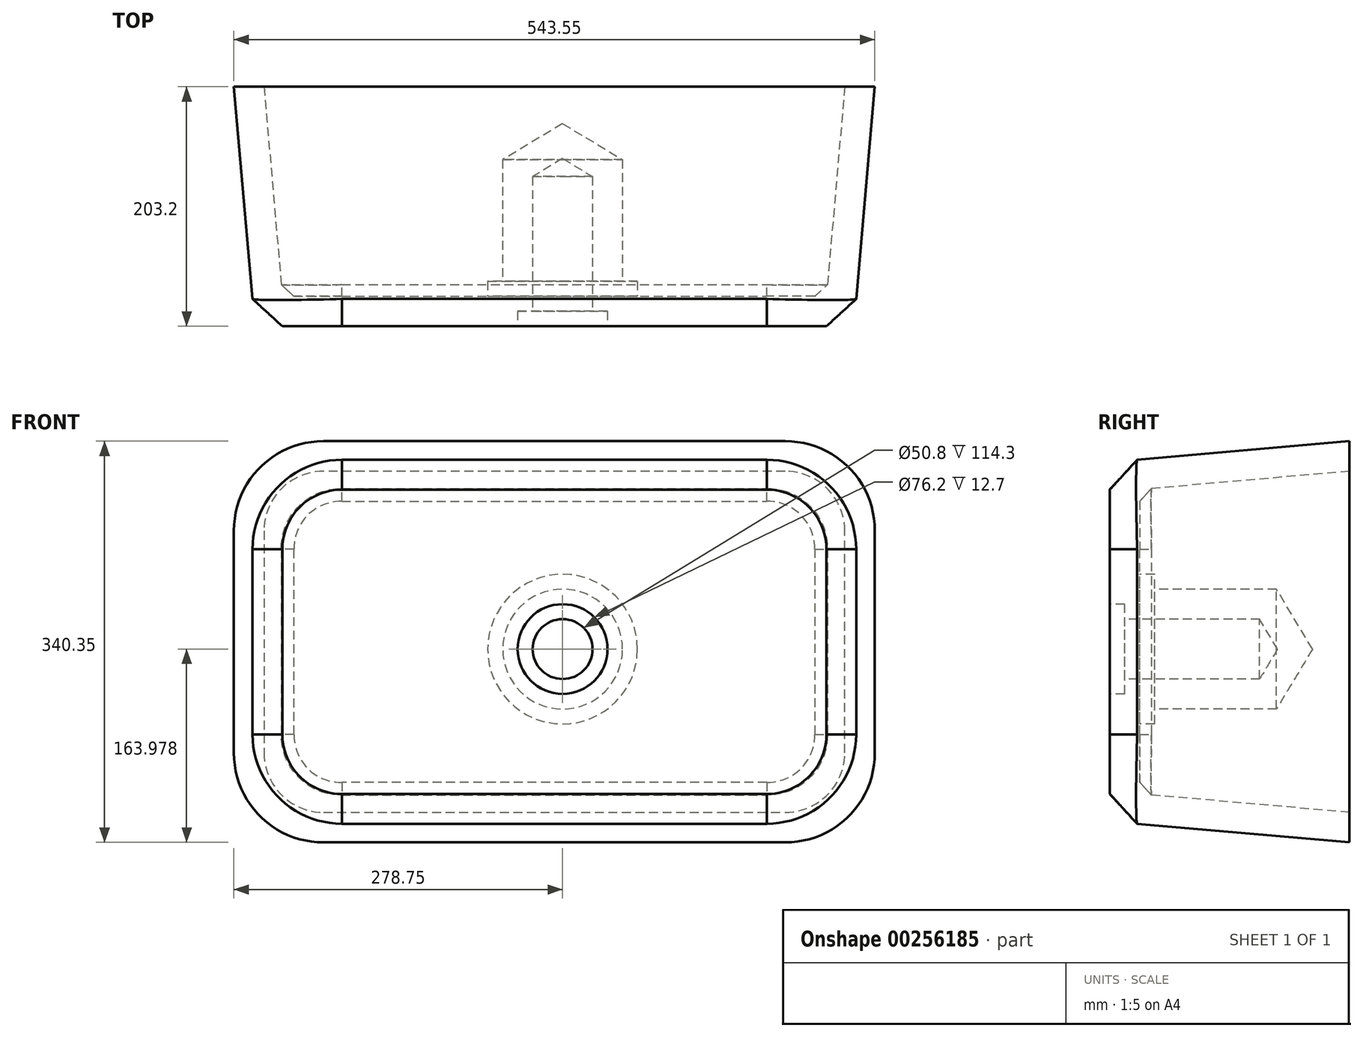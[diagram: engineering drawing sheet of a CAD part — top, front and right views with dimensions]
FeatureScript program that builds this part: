
annotation { "Feature Type Name" : "Feature", "Feature Type Description" : "" }
export const myFeature = defineFeature(function(context is Context, id is Id, definition is map)
    precondition{}
    {
        {
            var Q0;
            Q0=qCreatedBy(makeId("Front.planeOp"),FACE);
            var sketch = newSketch(context, id + "F0", { "sketchPlane" : qUnion([Q0])});
            skLineSegment(sketch, "E0.bottom", {"start": v(-260.97, 124.12) * mm, "end": v(247.03, 124.12) * mm});
            skLineSegment(sketch, "E0.top", {"start": v(-260.97, -180.68) * mm, "end": v(247.03, -180.68) * mm});
            skLineSegment(sketch, "E0.left", {"start": v(-260.97, 124.12) * mm, "end": v(-260.97, -180.68) * mm});
            skLineSegment(sketch, "E0.right", {"start": v(247.03, 124.12) * mm, "end": v(247.03, -180.68) * mm});
            skCircle(sketch, "E1", {"center": v(0, -34.47) * mm, "radius": 76.2 * mm});
            skSolve(sketch);
        }
        {
            var Q0;
            Q0=makeQuery(id+"F0.imprint","IMPRINT",FACE,{"disambiguationData":[TD([[makeQuery(id+"F0.imprint","IMPRINT",EDGE,{"derivedFrom":sQuery(id+"F0.wireOp",EDGE,"E0.bottom")}),-1.0]])]});
            var Q1;
            Q1=makeQuery(id+"F0.imprint","IMPRINT",FACE,{"disambiguationData":[TD([[makeQuery(id+"F0.imprint","IMPRINT",EDGE,{"derivedFrom":sQuery(id+"F0.wireOp",EDGE,"E1")}),1.0]])]});
            extrude(context, id + "F1", {"entities" : qUnion([Q0, Q1]), "oppositeDirection" : true, "depth" : 203.2 * mm, "hasDraft" : true, "draftAngle" : 5 * degree});
        }
        {
            var Q0;
            Q0=makeQuery(id+"F1.opExtrude","SWEPT_EDGE",EDGE,{"disambiguationData":[OSD([sQuery(id+"F0.wireOp",EDGE,"E0.bottom"),sQuery(id+"F0.wireOp",EDGE,"E0.left")])]});
            var Q1;
            Q1=makeQuery(id+"F1.opExtrude","SWEPT_EDGE",EDGE,{"disambiguationData":[OSD([sQuery(id+"F0.wireOp",EDGE,"E0.bottom"),sQuery(id+"F0.wireOp",EDGE,"E0.right")])]});
            var Q2;
            Q2=makeQuery(id+"F1.opExtrude","SWEPT_EDGE",EDGE,{"disambiguationData":[OSD([sQuery(id+"F0.wireOp",EDGE,"E0.top"),sQuery(id+"F0.wireOp",EDGE,"E0.left")])]});
            var Q3;
            Q3=makeQuery(id+"F1.opExtrude","SWEPT_EDGE",EDGE,{"disambiguationData":[OSD([sQuery(id+"F0.wireOp",EDGE,"E0.top"),sQuery(id+"F0.wireOp",EDGE,"E0.right")])]});
            fillet(context, id + "F2", {"entities" : qUnion([Q0, Q1, Q2, Q3]), "radius" : 76.2 * mm, "tangentPropagation" : true, "allowEdgeOverflow" : false});
        }
        {
            var Q0;
            Q0=makeQuery(id+"F1.opExtrude","CAP_EDGE",EDGE,{"disambiguationData":[OSD([sQuery(id+"F0.wireOp",EDGE,"E0.bottom")])],"isStart":true});
            chamfer(context, id + "F3", {"entities" : qUnion([Q0]), "width" : 25.4 * mm, "tangentPropagation" : true});
        }
        {
            var Q0;
            Q0=sQuery(id+"F0.wireOp",VERTEX,"E1.center");
            var Q1;
            Q1=makeQuery(id+"F1.opExtrude","SWEPT_BODY",BODY,{"disambiguationData":[OSD([sQuery(id+"F0.wireOp",EDGE,"E0.bottom"),sQuery(id+"F0.wireOp",EDGE,"E0.top"),sQuery(id+"F0.wireOp",EDGE,"E0.left"),sQuery(id+"F0.wireOp",EDGE,"E0.right")])]});
            hole(context, id + "F4", {"style" : HoleStyle.C_BORE, "endStyle" : HoleEndStyle.BLIND, "holeDiameter" : 50.8 * mm, "cBoreDiameter" : 76.2 * mm, "cBoreDepth" : 12.7 * mm, "holeDepth" : 127 * mm, "tappedDepth" : 12.7 * mm, "tapClearance" : 3, "locations" : qUnion([Q0]), "scope" : qUnion([Q1])});
        }
        {
            var Q0;
            Q0=makeQuery(id+"F1.opExtrude","CAP_FACE",FACE,{"disambiguationData":[OSD([sQuery(id+"F0.wireOp",EDGE,"E0.bottom"),sQuery(id+"F0.wireOp",EDGE,"E0.top"),sQuery(id+"F0.wireOp",EDGE,"E0.left"),sQuery(id+"F0.wireOp",EDGE,"E0.right")])],"isStart":false});
            shell(context, id + "F5", {"entities" : qUnion([Q0]), "thickness" : 25.4 * mm});
        }
    });
